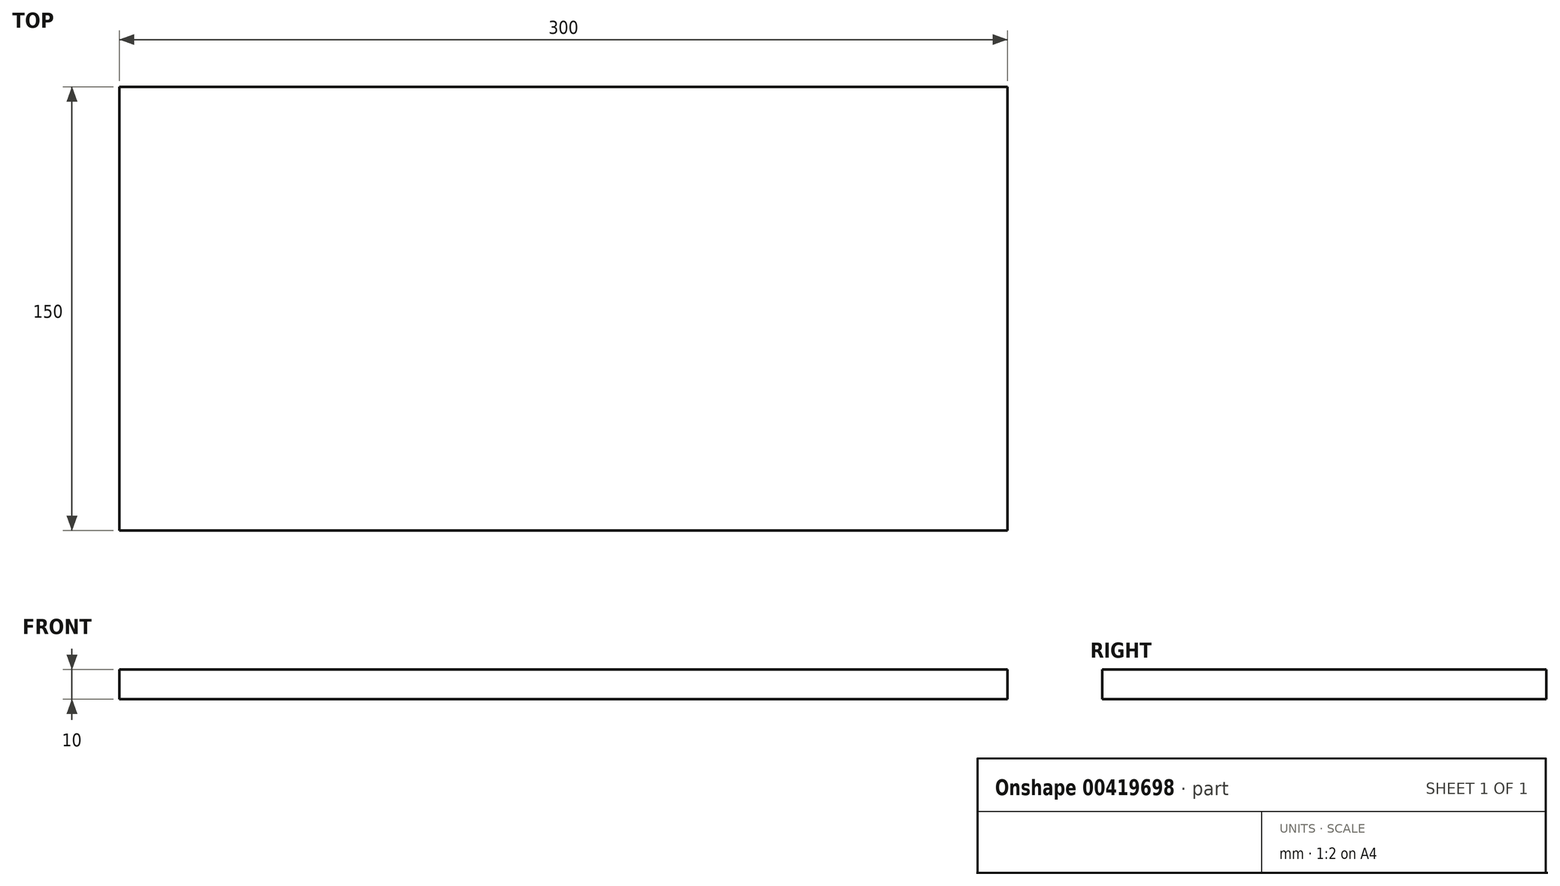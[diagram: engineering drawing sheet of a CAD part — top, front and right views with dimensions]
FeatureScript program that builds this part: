
annotation { "Feature Type Name" : "Feature", "Feature Type Description" : "" }
export const myFeature = defineFeature(function(context is Context, id is Id, definition is map)
    precondition{}
    {
        {
            var Q0;
            Q0=qCreatedBy(makeId("Top.planeOp"),FACE);
            var sketch = newSketch(context, id + "F0", { "sketchPlane" : qUnion([Q0])});
            skLineSegment(sketch, "E0.bottom", {"start": v(-121.91, 71.88) * mm, "end": v(178.09, 71.88) * mm});
            skLineSegment(sketch, "E0.top", {"start": v(-121.91, -78.12) * mm, "end": v(178.09, -78.12) * mm});
            skLineSegment(sketch, "E0.left", {"start": v(-121.91, 71.88) * mm, "end": v(-121.91, -78.12) * mm});
            skLineSegment(sketch, "E0.right", {"start": v(178.09, 71.88) * mm, "end": v(178.09, -78.12) * mm});
            skSolve(sketch);
        }
        {
            var Q0;
            Q0=makeQuery(id+"F0.imprint","IMPRINT",FACE,{"disambiguationData":[TD([[makeQuery(id+"F0.imprint","IMPRINT",EDGE,{"derivedFrom":sQuery(id+"F0.wireOp",EDGE,"E0.bottom")}),-1.0]])]});
            extrude(context, id + "F1", {"entities" : qUnion([Q0]), "depth" : 10 * mm});
        }
    });
